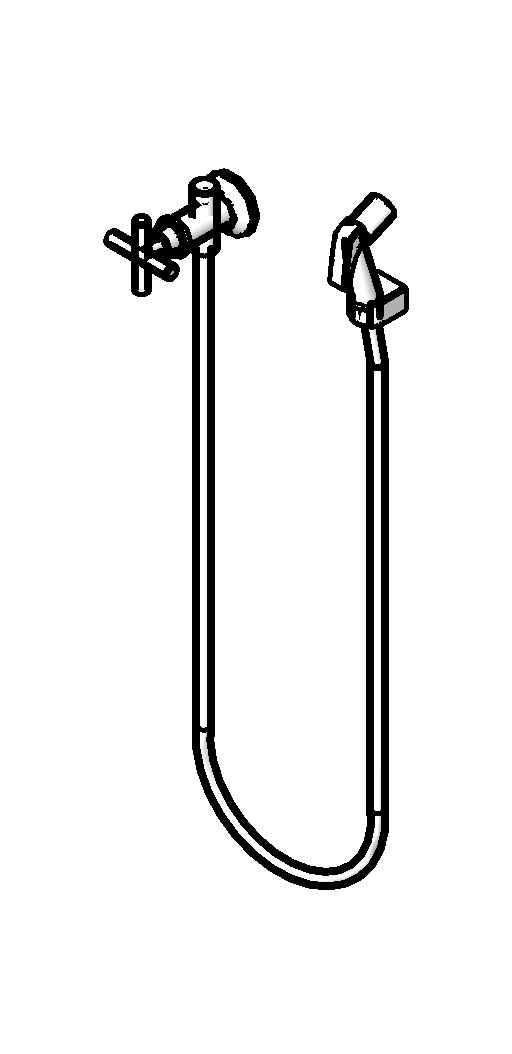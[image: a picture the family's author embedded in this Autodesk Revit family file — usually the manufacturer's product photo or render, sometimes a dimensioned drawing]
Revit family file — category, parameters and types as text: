
# Revit family: Deca_Ducha Higiênica Duna Classica_1984.C64.ACT.CR_Registro e Derivação
name_source: partatom
category: Plumbing Fixtures
revit_build: Autodesk Revit Architecture 2012 (Build: 20120126_0600(x64)
units: mm (PartAtom-declared; Revit-internal decimal feet)

## types (1)
- 1984.C64.ACT.CR_Comado CR10
    Aprovado por = Contino/quattroD
    Assembly Code = D2010710
    Atendimento ao Cliente = 0800-011-7073
    CWFU = 0
    Consumo = Varia com a pressão
    Criado por = Contino/quattroD
    Código = 1984.C64.ACT.CR
    Default Elevation = 1200 mm
    Description = Ducha higiênica com registro e derivação
    Diâmetro Água Fria = 15 mm  [stored 0.0492126 ft]
    Ducha Higiênica = Deca CR10 Cromado Metal
    Flow Pressure = 0.00 psi
    Informações Complementares = Mecanismo: 1/2 de volta
    Linha = Duna Clássica
    Louça/Metais = Metal
    Manufacturer = Deca
    Material = Deca_Latão Cromado e Plástico de Engenharia
    Model = 1984.C64.ACT.CR
    Norma = ABNT NBR 14877: 2002
    Peso Liquido (Kg) = 0.85
    Pressão = 2 A 40 mca
    Produto = Ducha higiênica com registro e derivação
    Raio Água Fria = 8 mm  [stored 0.0262467 ft]
    Segmento = Luxo
    URL = www.deca.com.br/produtos
    Variações de COR = Cromado (1984.C64.ACT.CR).

note: [stored X ft] marks values corroborated as IEEE doubles in the binary element streams (Revit-internal decimal feet)

## geometry (parser evidence)
native form markers: Blend x4, Sweep x2
no freeform markers — native parametric forms only
